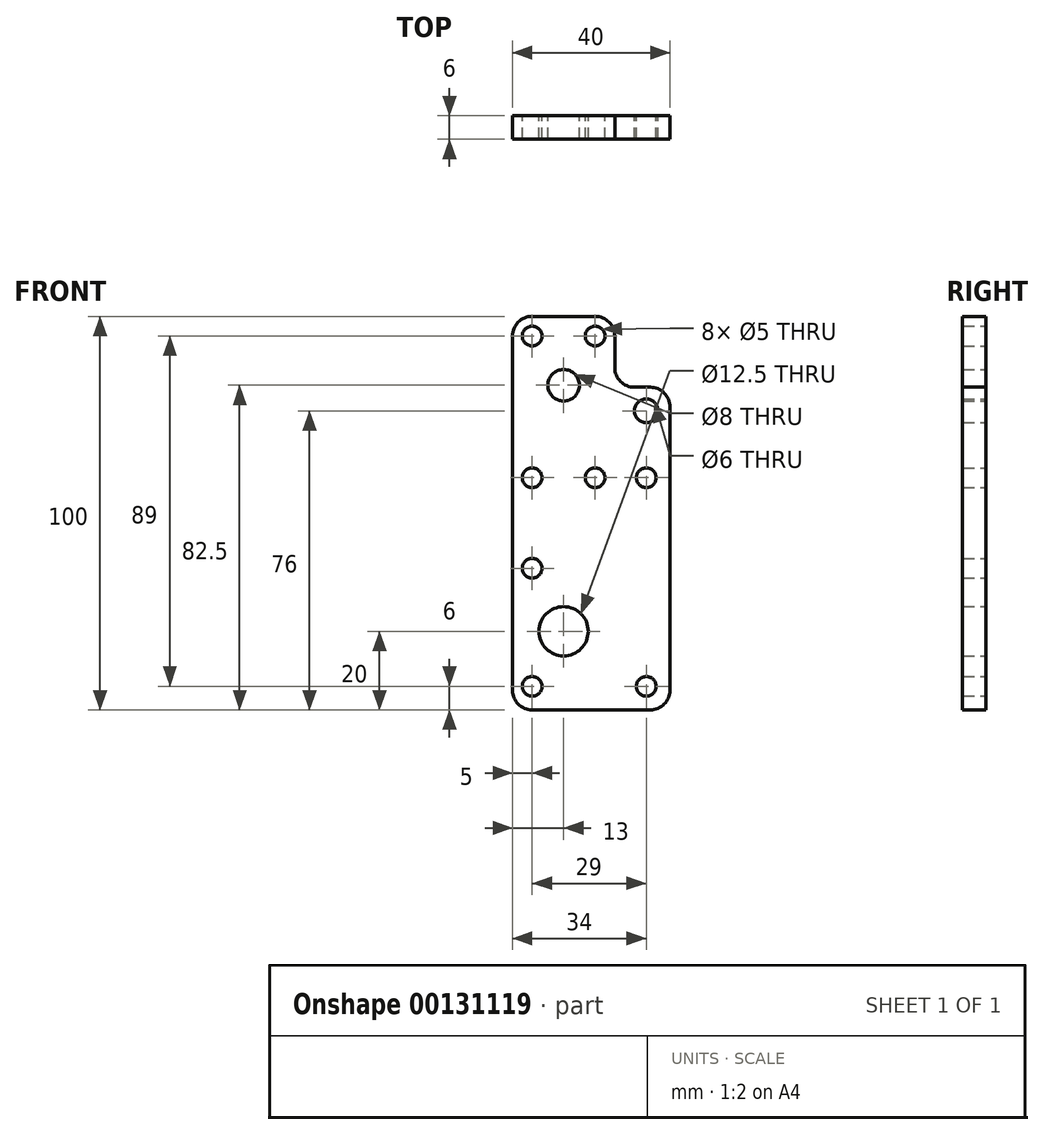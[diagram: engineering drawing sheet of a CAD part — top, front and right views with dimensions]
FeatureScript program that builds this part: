
annotation { "Feature Type Name" : "Feature", "Feature Type Description" : "" }
export const myFeature = defineFeature(function(context is Context, id is Id, definition is map)
    precondition{}
    {
        {
            var Q0;
            Q0=qCreatedBy(makeId("Front.planeOp"),FACE);
            var sketch = newSketch(context, id + "F0", { "sketchPlane" : qUnion([Q0])});
            skLineSegment(sketch, "E0.bottom", {"start": v(0, 27) * mm, "end": v(13, 27) * mm, "construction": true});
            skLineSegment(sketch, "E0.top", {"start": v(0, -27) * mm, "end": v(13, -27) * mm});
            skLineSegment(sketch, "E0.right", {"start": v(13, 27) * mm, "end": v(13, -27) * mm, "construction": true});
            skLineSegment(sketch, "E1", {"start": v(26, 55) * mm, "end": v(40, 55) * mm});
            skLineSegment(sketch, "E2", {"start": v(40, 55) * mm, "end": v(40, -27) * mm});
            skLineSegment(sketch, "E3", {"start": v(40, -27) * mm, "end": v(13, -27) * mm});
            skLineSegment(sketch, "E4", {"start": v(0, 27) * mm, "end": v(0, -27) * mm});
            skPoint(sketch, "E5", {"position": v(13, -7) * mm});
            skLineSegment(sketch, "E6", {"start": v(34, -27) * mm, "end": v(34, 55) * mm, "construction": true});
            skPoint(sketch, "E7", {"position": v(34, -21) * mm});
            skPoint(sketch, "E8", {"position": v(34, 32) * mm});
            skLineSegment(sketch, "E9", {"start": v(5, -27) * mm, "end": v(5, 32) * mm, "construction": true});
            skPoint(sketch, "E10", {"position": v(5, 32) * mm});
            skLineSegment(sketch, "E11", {"start": v(5, 32) * mm, "end": v(21, 32) * mm, "construction": true});
            skPoint(sketch, "E12", {"position": v(21, 32) * mm});
            skPoint(sketch, "E13", {"position": v(5, -21) * mm});
            skPoint(sketch, "E14", {"position": v(5, 9) * mm});
            skLineSegment(sketch, "E15", {"start": v(5, 9) * mm, "end": v(17, 9) * mm, "construction": true});
            skPoint(sketch, "E16", {"position": v(17, 9) * mm});
            skPoint(sketch, "E17", {"position": v(26, 55) * mm});
            skLineSegment(sketch, "E18", {"start": v(26, 55) * mm, "end": v(26, 73) * mm});
            skLineSegment(sketch, "E19", {"start": v(26, 73) * mm, "end": v(0, 73) * mm});
            skPoint(sketch, "E20.orphan", {"position": v(0, 55) * mm});
            skLineSegment(sketch, "E21", {"start": v(0, 73) * mm, "end": v(0, 27) * mm});
            skPoint(sketch, "E22", {"position": v(5, 68) * mm});
            skPoint(sketch, "E23", {"position": v(21, 68) * mm});
            skPoint(sketch, "E24", {"position": v(13, 55.5) * mm});
            skPoint(sketch, "E25", {"position": v(34, 49) * mm});
            skSolve(sketch);
        }
        {
            var Q0;
            Q0=makeQuery(id+"F0.imprint","IMPRINT",FACE,{"disambiguationData":[TD([[makeQuery(id+"F0.imprint","IMPRINT",EDGE,{"derivedFrom":sQuery(id+"F0.wireOp",EDGE,"E0.top")}),1.0]])]});
            extrude(context, id + "F1", {"entities" : qUnion([Q0]), "depth" : 6 * mm});
        }
        {
            var Q0;
            Q0=sQuery(id+"F0.wireOp",VERTEX,"E5");
            var Q1;
            Q1=makeQuery(id+"F1.opExtrude","SWEPT_BODY",BODY,{"disambiguationData":[OSD([sQuery(id+"F0.wireOp",EDGE,"E0.top"),sQuery(id+"F0.wireOp",EDGE,"E1"),sQuery(id+"F0.wireOp",EDGE,"E2"),sQuery(id+"F0.wireOp",EDGE,"E3"),sQuery(id+"F0.wireOp",EDGE,"E4")])]});
            hole(context, id + "F2", {"style" : HoleStyle.SIMPLE, "endStyle" : HoleEndStyle.THROUGH, "oppositeDirection" : true, "holeDiameter" : 12.5 * mm, "locations" : qUnion([Q0]), "scope" : qUnion([Q1]), "isTappedThrough" : true});
        }
        {
            var Q0;
            Q0=sQuery(id+"F0.wireOp",VERTEX,"E7");
            var Q1;
            Q1=sQuery(id+"F0.wireOp",VERTEX,"E8");
            var Q2;
            Q2=makeQuery(id+"F1.opExtrude","SWEPT_BODY",BODY,{"disambiguationData":[OSD([sQuery(id+"F0.wireOp",EDGE,"E0.top"),sQuery(id+"F0.wireOp",EDGE,"E1"),sQuery(id+"F0.wireOp",EDGE,"E2"),sQuery(id+"F0.wireOp",EDGE,"E3"),sQuery(id+"F0.wireOp",EDGE,"E4")])]});
            hole(context, id + "F3", {"style" : HoleStyle.SIMPLE, "endStyle" : HoleEndStyle.THROUGH, "oppositeDirection" : true, "holeDiameter" : 5 * mm, "locations" : qUnion([Q0, Q1]), "scope" : qUnion([Q2]), "isTappedThrough" : true});
        }
        {
            var Q0;
            Q0=sQuery(id+"F0.wireOp",VERTEX,"E10");
            var Q1;
            Q1=sQuery(id+"F0.wireOp",VERTEX,"E12");
            var Q2;
            Q2=makeQuery(id+"F1.opExtrude","SWEPT_BODY",BODY,{"disambiguationData":[OSD([sQuery(id+"F0.wireOp",EDGE,"E0.top"),sQuery(id+"F0.wireOp",EDGE,"E1"),sQuery(id+"F0.wireOp",EDGE,"E2"),sQuery(id+"F0.wireOp",EDGE,"E3"),sQuery(id+"F0.wireOp",EDGE,"E4")])]});
            hole(context, id + "F4", {"style" : HoleStyle.SIMPLE, "endStyle" : HoleEndStyle.THROUGH, "oppositeDirection" : true, "holeDiameter" : 5 * mm, "locations" : qUnion([Q0, Q1]), "scope" : qUnion([Q2]), "isTappedThrough" : true});
        }
        {
            var Q0;
            Q0=sQuery(id+"F0.wireOp",VERTEX,"E13");
            var Q1;
            Q1=sQuery(id+"F0.wireOp",VERTEX,"E14");
            var Q2;
            Q2=makeQuery(id+"F1.opExtrude","SWEPT_BODY",BODY,{"disambiguationData":[OSD([sQuery(id+"F0.wireOp",EDGE,"E0.top"),sQuery(id+"F0.wireOp",EDGE,"E1"),sQuery(id+"F0.wireOp",EDGE,"E2"),sQuery(id+"F0.wireOp",EDGE,"E3"),sQuery(id+"F0.wireOp",EDGE,"E4")])]});
            hole(context, id + "F5", {"style" : HoleStyle.SIMPLE, "endStyle" : HoleEndStyle.THROUGH, "oppositeDirection" : true, "holeDiameter" : 5 * mm, "locations" : qUnion([Q0, Q1]), "scope" : qUnion([Q2]), "isTappedThrough" : true});
        }
        {
            var Q0;
            Q0=sQuery(id+"F0.wireOp",VERTEX,"E22");
            var Q1;
            Q1=sQuery(id+"F0.wireOp",VERTEX,"E23");
            var Q2;
            Q2=makeQuery(id+"F1.opExtrude","SWEPT_BODY",BODY,{"disambiguationData":[OSD([sQuery(id+"F0.wireOp",EDGE,"E0.top"),sQuery(id+"F0.wireOp",EDGE,"E1"),sQuery(id+"F0.wireOp",EDGE,"E2"),sQuery(id+"F0.wireOp",EDGE,"E3"),sQuery(id+"F0.wireOp",EDGE,"E4"),sQuery(id+"F0.wireOp",EDGE,"E18"),sQuery(id+"F0.wireOp",EDGE,"E19"),sQuery(id+"F0.wireOp",EDGE,"E21")])]});
            hole(context, id + "F6", {"style" : HoleStyle.SIMPLE, "endStyle" : HoleEndStyle.THROUGH, "oppositeDirection" : true, "holeDiameter" : 5 * mm, "locations" : qUnion([Q0, Q1]), "scope" : qUnion([Q2]), "isTappedThrough" : true});
        }
        {
            var Q0;
            Q0=makeQuery(id+"F1.opExtrude","SWEPT_EDGE",EDGE,{"disambiguationData":[OSD([sQuery(id+"F0.wireOp",EDGE,"E18"),sQuery(id+"F0.wireOp",EDGE,"E19")])]});
            var Q1;
            Q1=makeQuery(id+"F1.opExtrude","SWEPT_EDGE",EDGE,{"disambiguationData":[OSD([sQuery(id+"F0.wireOp",EDGE,"E19"),sQuery(id+"F0.wireOp",EDGE,"E21")])]});
            var Q2;
            Q2=makeQuery(id+"F1.opExtrude","SWEPT_EDGE",EDGE,{"disambiguationData":[OSD([sQuery(id+"F0.wireOp",EDGE,"E1"),sQuery(id+"F0.wireOp",EDGE,"E2")])]});
            var Q3;
            Q3=makeQuery(id+"F1.opExtrude","SWEPT_EDGE",EDGE,{"disambiguationData":[OSD([sQuery(id+"F0.wireOp",EDGE,"E1"),sQuery(id+"F0.wireOp",EDGE,"E18")])]});
            var Q4;
            Q4=makeQuery(id+"F1.opExtrude","SWEPT_EDGE",EDGE,{"disambiguationData":[OSD([sQuery(id+"F0.wireOp",EDGE,"E2"),sQuery(id+"F0.wireOp",EDGE,"E3")])]});
            var Q5;
            Q5=makeQuery(id+"F1.opExtrude","SWEPT_EDGE",EDGE,{"disambiguationData":[OSD([sQuery(id+"F0.wireOp",EDGE,"E0.top"),sQuery(id+"F0.wireOp",EDGE,"E4")])]});
            fillet(context, id + "F7", {"entities" : qUnion([Q0, Q1, Q2, Q3, Q4, Q5]), "radius" : 5 * mm, "tangentPropagation" : true, "allowEdgeOverflow" : false});
        }
        {
            var Q0;
            Q0=sQuery(id+"F0.wireOp",VERTEX,"E24");
            var Q1;
            Q1=makeQuery(id+"F1.opExtrude","SWEPT_BODY",BODY,{"disambiguationData":[OSD([sQuery(id+"F0.wireOp",EDGE,"E0.top"),sQuery(id+"F0.wireOp",EDGE,"E1"),sQuery(id+"F0.wireOp",EDGE,"E2"),sQuery(id+"F0.wireOp",EDGE,"E3"),sQuery(id+"F0.wireOp",EDGE,"E4"),sQuery(id+"F0.wireOp",EDGE,"E18"),sQuery(id+"F0.wireOp",EDGE,"E19"),sQuery(id+"F0.wireOp",EDGE,"E21")])]});
            hole(context, id + "F8", {"style" : HoleStyle.SIMPLE, "endStyle" : HoleEndStyle.BLIND, "oppositeDirection" : true, "holeDiameter" : 8 * mm, "holeDepth" : 20 * mm, "locations" : qUnion([Q0]), "scope" : qUnion([Q1])});
        }
        {
            var Q0;
            Q0=sQuery(id+"F0.wireOp",VERTEX,"E25");
            var Q1;
            Q1=makeQuery(id+"F1.opExtrude","SWEPT_BODY",BODY,{"disambiguationData":[OSD([sQuery(id+"F0.wireOp",EDGE,"E0.top"),sQuery(id+"F0.wireOp",EDGE,"E1"),sQuery(id+"F0.wireOp",EDGE,"E2"),sQuery(id+"F0.wireOp",EDGE,"E3"),sQuery(id+"F0.wireOp",EDGE,"E4"),sQuery(id+"F0.wireOp",EDGE,"E18"),sQuery(id+"F0.wireOp",EDGE,"E19"),sQuery(id+"F0.wireOp",EDGE,"E21")])]});
            hole(context, id + "F9", {"style" : HoleStyle.SIMPLE, "endStyle" : HoleEndStyle.THROUGH, "oppositeDirection" : true, "holeDiameter" : 6 * mm, "locations" : qUnion([Q0]), "scope" : qUnion([Q1]), "isTappedThrough" : true});
        }
    });
